# Revit family: PRD_FrankeWS_ShwrHds_ShowerJetNozzle_AQRM706_AQRM707
name_source: partatom
category: Specialty Equipment
revit_build: Autodesk Revit 2018 (Build: 20190510_1515(x64)
units: mm (PartAtom-declared; Revit-internal decimal feet)

## family parameters
Always vertical = Yes
Cut with Voids When Loaded = No
OmniClass Number = 23.45.05.14.17
OmniClass Title = Showers
Part Type = Normal
Room Calculation Point = No
Round Connector Dimension = Use Diameter
Shared = No
Work Plane-Based = Yes

## types (2) — shared parameters
AdjustableTiltAngle = No
AssetType = Fixed
BodyMaterial = PRD_AR_ChromatedBrass_HighPolished
Category = Pr_40_20_87_76, Shower heads
Default Elevation = 1219 mm
DiameterNominal = 15  [stored 0.0492126 ft]
DrainSize = 15 mm  [stored 0.0492126 ft]
DurationUnit = year
Finish = polished chromium-plated
GrossWeight = 0.14 kg
HasTray = FALSE
IfcExportAs = IfcSanitaryTerminalType
IfcExportType = SHOWER
InletSize = DN 15
Manufacturer = KWC Group AG
ManufacturerName = KWC Group AG
ManufacturerURL = www.kwc.com
Material = brass
MinimumFlowPressure = 1.50 bar
NBSDescription = Shower heads
NBSReference = 45-35-70/333
NetWeight = 0.13 kg
NominalDepth = 30 mm  [stored 0.0984252 ft]
NominalHeight = 52 mm
NominalWidth = 30 mm  [stored 0.0984252 ft]
ProductInformation = https://pim.kwc.com
ShowerHeadDescription = Jet shower head
ShowerType = Individual
SoundInsulation = No
TailorMade = No
Type = Shower head
TypeOfConnection = Cantilever connection
TypeOfShowerHead = Jet shower head
URL = www.kwc.com
Uniclass2015Code = Pr_40_20_87_76
Uniclass2015Title = Shower heads
Uniclass2015Version = Products v1.23
Version = 1
WarrantyDurationUnit = year

## per-type parameters (varying)
| type | BIMObjectName | Description | Features | ModelNumber | Name | ProductCode | VolumeFlowRate |
| AQRM706 | PRD_AR_ShowerHeads_ShowerJetNozzle_AQRM706 | Jet shower head DN 15, polished chromium-plated brass, connection G 1/2. With flow controller 9.0 l/min. | flow controller 9.0 l/min | 2000100899 | Shower jet nozzle AQRM706 | 210.0636.617 | 0.15 l/s at 3 bar |
| AQRM707 | PRD_AR_ShowerHeads_ShowerJetNozzle_AQRM707 | Jet shower head DN 15, polished chromium-plated brass, connection G 1/2. With flow controller 12.0 l/min. | flow controller 12.0 l/min | 2000100900 | Shower jet nozzle AQRM707 | 210.0636.618 | 0.20 l/s at 3 bar |

note: column(s) folded — value = type name in every type: Model, ModelReference

note: [stored X ft] marks values corroborated as IEEE doubles in the binary element streams (Revit-internal decimal feet)

## geometry (parser evidence)
native form markers: Sweep x3
no freeform markers — native parametric forms only
